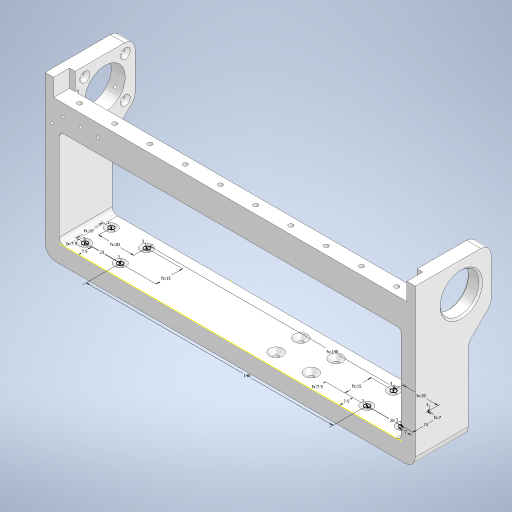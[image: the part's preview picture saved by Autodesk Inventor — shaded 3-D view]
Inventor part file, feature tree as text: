
AUTODESK INVENTOR PART (.ipt)
format: ipt  version: 2024.1 (Build 281209000, 209)  size: 493,568 bytes
history: native  units: in
note: dims shown in document units (in); Inventor stores cm internally (conversion verified against a paired STEP export)
features: extrude x11, sketch x11, chamfer x5, fillet x4
ambient origin geometry x8: Origin, YZ Plane, XZ Plane, XY Plane, X Axis, Y Axis, Z Axis, Center Point
bodies: Solid1 (feature_tree)
feature tree (31):
  extrude  "Extrusion1"  Depth=3.5433in
  extrude  "Extrusion2"  Depth=0.315in
  extrude  "Extrusion3"  Depth=0.3937in
  chamfer  "Chamfer1"  Distance=1.1811in
  extrude  "Extrusion9"  Depth=0.1181in
  chamfer  "Chamfer4"  Distance=0.2953in
  extrude  "Extrusion12"  Depth=0.3937in
  extrude  "Extrusion13"  Depth=0.3937in
  fillet  "Fillet3"  Radius=0.7874in
  extrude  "Extrusion14"  Depth=0.3937in
  extrude  "Extrusion15"  Depth=0.3937in
  chamfer  "Chamfer9"  Distance=0.7874in
  fillet  "Fillet4"  Radius=0.7874in
  fillet  "Fillet5"  Radius=0.2756in
  fillet  "Fillet6"  Radius=0.5906in
  extrude  "Extrusion17"  Depth=0.3937in
  chamfer  "Chamfer10"  Distance=0.5906in
  extrude  "Extrusion18"  Depth=0.3937in
  chamfer  "Chamfer11"  Distance=5.5118in
  extrude  "Extrusion19"  Depth=0.3937in
  sketch  "Sketch1"  dims[d0=8.2677in d1=3.5433in]
  sketch  "Sketch2"  dims[d2=1.1811in d3=0.0in d4=0.315in]
  sketch  "Sketch3"  dims[d5=0.315in d6=0.3937in d7=1.1811in d8=0.0in]
  sketch  "Sketch9"  dims[d9=0.1181in d10=0.1181in]
  sketch  "Sketch12"  dims[d11=0.1181in]
  sketch  "Sketch13"  dims[d12=0.1181in]
  sketch  "Sketch14"  dims[d13=0.1181in]
  sketch  "Sketch15"  dims[d14=0.1181in]
  sketch  "Sketch17"  dims[d15=0.1181in]
  sketch  "Sketch18"  dims[d16=0.1181in]
  sketch  "Sketch19"  dims[d18=0.2953in d19=0.2953in d20=0.2953in d21=0.2953in d22=0.7874in d23=0.7874in d24=0.2756in d25=0.7874in d26=0.7874in d27=0.2756in d28=0.5906in d29=0.5906in d30=0.5906in d31=0.5906in d33=5.5118in d34=5.5118in d35=1.1811in d36=0.0in d37=0.0709in d38=0.125in d39=45.0deg d74=1.1811in d75=1.1811in d76=0.5118in d77=0.0in d78=0.5118in d79=0.0787in d80=45.0deg d90=0.315in d97=0.3543in d98=0.5906in d99=0.3937in d100=7.6378in d101=0.0in d102=0.9055in d103=0.6693in d104=0.6693in d105=7.9528in d106=0.0in d107=0.0787in d108=0.3543in d109=0.126in d110=0.126in d111=0.3937in d112=0.0in d116=0.3976in d117=0.1772in d118=3.937in d120=0.7874in d121=0.3937in d123=0.3937in d125=0.5906in d126=0.0in d127=0.1024in d128=0.0984in d129=0.0984in d130=0.0984in d131=0.0984in d132=0.4528in d133=0.4528in d134=0.4528in d135=0.4528in d136=0.4528in d137=0.4528in d138=0.4528in d139=0.4528in d149=0.063in d150=0.0787in d151=45.0deg d152=0.1181in d153=0.2362in d154=0.2362in d155=0.1181in d156=0.1181in d157=0.1181in d158=0.1181in d159=0.315in d160=0.315in d161=0.315in d162=0.315in d163=0.7874in d164=0.7874in d165=4.5276in d166=4.5276in d167=0.3937in d168=0.0in d169=0.0906in d170=0.0787in d171=45.0deg d172=0.874in d173=0.0in d174=0.0in d175=0.0394in d176=0.0787in d177=45.0deg d178=0.063in d179=0.063in d180=0.063in d181=0.2756in d182=0.2756in d183=0.2756in d184=0.3937in d185=0.3937in d186=0.3937in d187=0.0in d188=0.0in d189=0.063in d190=0.1575in d191=0.5118in]
